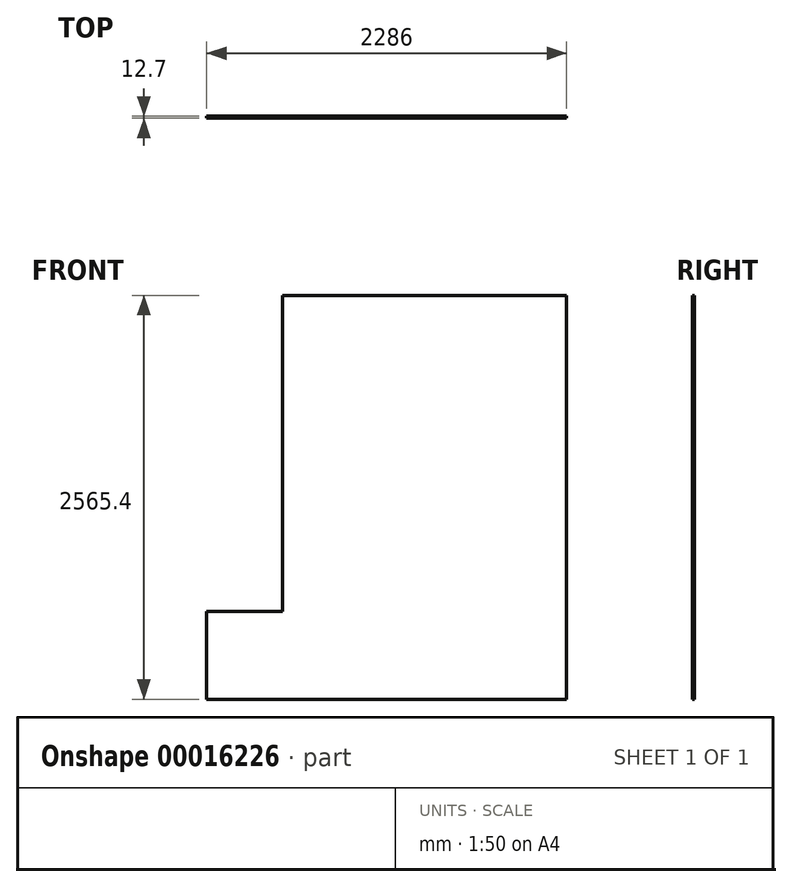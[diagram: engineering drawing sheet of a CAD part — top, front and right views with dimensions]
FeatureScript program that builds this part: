
annotation { "Feature Type Name" : "Feature", "Feature Type Description" : "" }
export const myFeature = defineFeature(function(context is Context, id is Id, definition is map)
    precondition{}
    {
        {
            var Q0;
            Q0=qCreatedBy(makeId("Front.planeOp"),FACE);
            var sketch = newSketch(context, id + "F0", { "sketchPlane" : qUnion([Q0])});
            skLineSegment(sketch, "E0.rect.left", {"start": v(-552.15, -769.45) * mm, "end": v(-552.15, 1237.15) * mm});
            skLineSegment(sketch, "E0.rect.right", {"start": v(1251.25, -1328.25) * mm, "end": v(1251.25, 1237.15) * mm});
            skPoint(sketch, "E0.rect.middle", {"position": v(349.55, -45.55) * mm});
            skLineSegment(sketch, "E1", {"start": v(-552.15, -769.45) * mm, "end": v(-1034.75, -769.45) * mm});
            skLineSegment(sketch, "E2", {"start": v(-1034.75, -769.45) * mm, "end": v(-1034.75, -1328.25) * mm});
            skLineSegment(sketch, "E3", {"start": v(-1034.75, -1328.25) * mm, "end": v(1251.25, -1328.25) * mm});
            skLineSegment(sketch, "E4.right", {"start": v(-552.15, 1237.15) * mm, "end": v(-552.15, 609.93) * mm});
            skLineSegment(sketch, "E5", {"start": v(-552.15, 1237.15) * mm, "end": v(1251.25, 1237.15) * mm});
            skSolve(sketch);
        }
        {
            var Q0;
            Q0=makeQuery(id+"F0.imprint","IMPRINT",FACE,{"disambiguationData":[TD([[makeQuery(id+"F0.imprint","IMPRINT",EDGE,{"derivedFrom":sQuery(id+"F0.wireOp",EDGE,"E0.rect.left")}),-1.0]])]});
            extrude(context, id + "F1", {"entities" : qUnion([Q0]), "oppositeDirection" : true, "depth" : 12.7 * mm});
        }
    });
